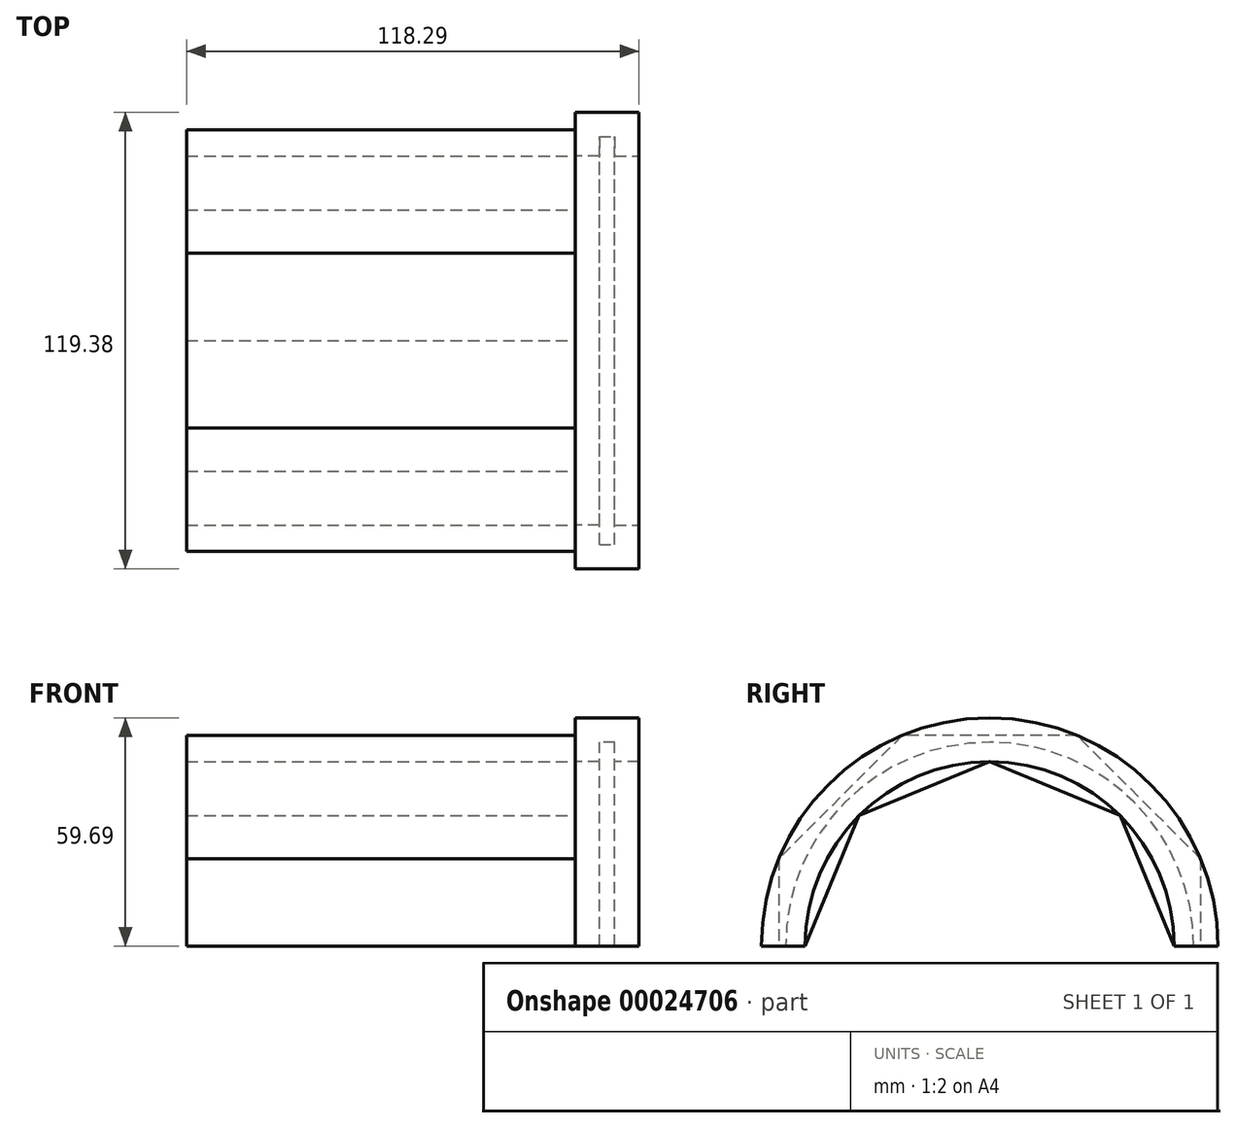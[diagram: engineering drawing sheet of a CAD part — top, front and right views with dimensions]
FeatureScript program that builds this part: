
annotation { "Feature Type Name" : "Feature", "Feature Type Description" : "" }
export const myFeature = defineFeature(function(context is Context, id is Id, definition is map)
    precondition{}
    {
        {
            var Q0;
            Q0=qCreatedBy(makeId("Top.planeOp"),FACE);
            var sketch = newSketch(context, id + "F0", { "sketchPlane" : qUnion([Q0])});
            skLineSegment(sketch, "E0", {"start": v(-31.66, 53.34) * mm, "end": v(-27.67, 53.34) * mm});
            skLineSegment(sketch, "E1.bottom", {"start": v(-31.66, 53.34) * mm, "end": v(-38, 53.34) * mm});
            skLineSegment(sketch, "E1.top", {"start": v(-31.66, 48.26) * mm, "end": v(-38, 48.26) * mm});
            skLineSegment(sketch, "E1.left", {"start": v(-31.66, 53.34) * mm, "end": v(-31.66, 48.26) * mm});
            skLineSegment(sketch, "E1.right", {"start": v(-38, 53.34) * mm, "end": v(-38, 48.26) * mm});
            skLineSegment(sketch, "E2.bottom", {"start": v(-27.67, 53.34) * mm, "end": v(-21.32, 53.34) * mm});
            skLineSegment(sketch, "E2.top", {"start": v(-27.67, 48.26) * mm, "end": v(-21.32, 48.26) * mm});
            skLineSegment(sketch, "E2.left", {"start": v(-27.67, 53.34) * mm, "end": v(-27.67, 48.26) * mm});
            skLineSegment(sketch, "E2.right", {"start": v(-21.32, 53.34) * mm, "end": v(-21.32, 48.26) * mm});
            skLineSegment(sketch, "E3.bottom", {"start": v(-38, 53.34) * mm, "end": v(-21.32, 53.34) * mm});
            skLineSegment(sketch, "E3.top", {"start": v(-38, 59.7) * mm, "end": v(-21.32, 59.7) * mm});
            skLineSegment(sketch, "E3.left", {"start": v(-38, 53.34) * mm, "end": v(-38, 59.7) * mm});
            skLineSegment(sketch, "E3.right", {"start": v(-21.32, 53.34) * mm, "end": v(-21.32, 59.7) * mm});
            skLineSegment(sketch, "E4", {"start": v(-17.34, 0) * mm, "end": v(0, 0) * mm});
            skSolve(sketch);
        }
        {
            var Q0;
            Q0=qSketchRegion(id+"F0",true);
            var Q1;
            Q1=sQuery(id+"F0.wireOp",EDGE,"E4");
            revolve(context, id + "F1", {"entities" : qUnion([Q0]), "axis" : qUnion([Q1]), "revolveType" : RevolveType.ONE_DIRECTION, "angle" : 180 * degree});
        }
        {
            var Q0;
            Q0=makeQuery(id+"F1.opRevolve","SWEPT_FACE",FACE,{"disambiguationData":[OSD([sQuery(id+"F0.wireOp",EDGE,"E1.right"),sQuery(id+"F0.wireOp",EDGE,"E3.left")])]});
            var sketch = newSketch(context, id + "F2", { "sketchPlane" : qUnion([Q0])});
            skLineSegment(sketch, "E5", {"start": v(-55.15, 22.84) * mm, "end": v(-22.84, 55.15) * mm});
            skLineSegment(sketch, "E6", {"start": v(-22.84, 55.15) * mm, "end": v(22.84, 55.15) * mm});
            skLineSegment(sketch, "E7", {"start": v(22.84, 55.15) * mm, "end": v(55.15, 22.84) * mm});
            skLineSegment(sketch, "E8", {"start": v(55.15, 22.84) * mm, "end": v(55.15, 0) * mm});
            skLineSegment(sketch, "E9", {"start": v(-55.15, 22.84) * mm, "end": v(-55.15, 0) * mm});
            skLineSegment(sketch, "E10", {"start": v(-48.26, 0) * mm, "end": v(-34.12, 34.12) * mm});
            skLineSegment(sketch, "E11", {"start": v(-34.12, 34.12) * mm, "end": v(0, 48.26) * mm});
            skLineSegment(sketch, "E12", {"start": v(0, 48.26) * mm, "end": v(34.12, 34.12) * mm});
            skLineSegment(sketch, "E13", {"start": v(34.12, 34.12) * mm, "end": v(48.26, 0) * mm});
            skSolve(sketch);
        }
        {
            var Q0;
            Q0=qSketchRegion(id+"F2",true);
            var Q1;
            {var subQ19=sQuery(id+"F2.wireOp",EDGE,"E5");Q1=makeQuery(id+"F2.imprint","IMPRINT",FACE,{"disambiguationData":[TD([[makeQuery(id+"F2.imprint","IMPRINT",EDGE,{"derivedFrom":subQ19}),-1.0]])]});}
            var Q2;
            {var subQ1=sQuery(id+"F2.wireOp",EDGE,"E12");Q2=makeQuery(id+"F2.imprint","IMPRINT",FACE,{"disambiguationData":[TD([[makeQuery(id+"F2.imprint","IMPRINT",EDGE,{"derivedFrom":subQ1}),1.0]])]});}
            var Q3;
            {var subQ1=sQuery(id+"F2.wireOp",EDGE,"E11");Q3=makeQuery(id+"F2.imprint","IMPRINT",FACE,{"disambiguationData":[TD([[makeQuery(id+"F2.imprint","IMPRINT",EDGE,{"derivedFrom":subQ1}),1.0]])]});}
            var Q4;
            {var subQ2=sQuery(id+"F2.wireOp",EDGE,"E10");Q4=makeQuery(id+"F2.imprint","IMPRINT",FACE,{"disambiguationData":[TD([[makeQuery(id+"F2.imprint","IMPRINT",EDGE,{"derivedFrom":subQ2}),1.0]])]});}
            var Q5;
            {var subQ2=sQuery(id+"F2.wireOp",EDGE,"E13");Q5=makeQuery(id+"F2.imprint","IMPRINT",FACE,{"disambiguationData":[TD([[makeQuery(id+"F2.imprint","IMPRINT",EDGE,{"derivedFrom":subQ2}),1.0]])]});}
            extrude(context, id + "F3", {"entities" : qUnion([Q0, Q1, Q2, Q3, Q4, Q5]), "operationType" : NewBodyOperationType.ADD, "depth" : 101.6 * mm});
        }
    });
